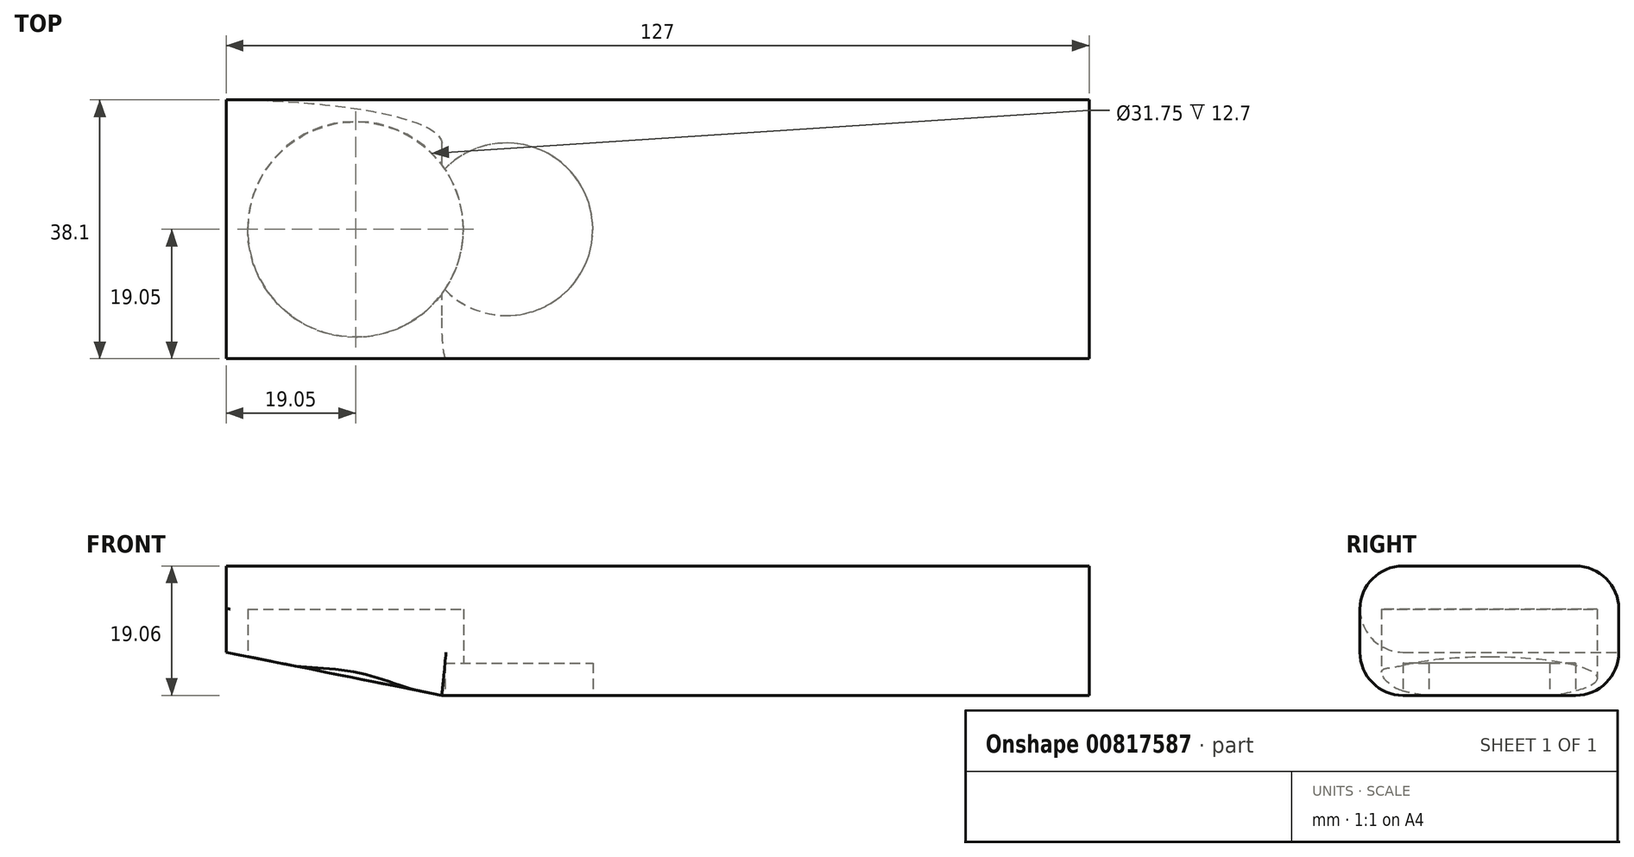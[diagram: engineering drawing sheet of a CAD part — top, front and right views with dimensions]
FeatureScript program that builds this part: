
annotation { "Feature Type Name" : "Feature", "Feature Type Description" : "" }
export const myFeature = defineFeature(function(context is Context, id is Id, definition is map)
    precondition{}
    {
        {
            var Q0;
            Q0=qCreatedBy(makeId("Top.planeOp"),FACE);
            var sketch = newSketch(context, id + "F0", { "sketchPlane" : qUnion([Q0])});
            skLineSegment(sketch, "E0.bottom", {"start": v(-63.5, 19.05) * mm, "end": v(63.5, 19.05) * mm});
            skLineSegment(sketch, "E0.top", {"start": v(-63.5, -19.05) * mm, "end": v(63.5, -19.05) * mm});
            skLineSegment(sketch, "E0.left", {"start": v(-63.5, 19.05) * mm, "end": v(-63.5, -19.05) * mm});
            skLineSegment(sketch, "E0.right", {"start": v(63.5, 19.05) * mm, "end": v(63.5, -19.05) * mm});
            skLineSegment(sketch, "E1", {"start": v(-63.5, 19.05) * mm, "end": v(63.5, -19.05) * mm, "construction": true});
            skSolve(sketch);
        }
        {
            var Q0;
            Q0 = qSketchRegion(id + "F0", true);
            extrude(context, id + "F1", {"entities" : qUnion([Q0]), "endBound" : BoundingType.SYMMETRIC, "depth" : 19.05 * mm, "offsetDistance" : 25.4 * mm});
        }
        {
            var Q0;
            Q0=makeQuery(id+"F1.opExtrude","CAP_FACE",FACE,{"disambiguationData":[OSD([sQuery(id+"F0.wireOp",EDGE,"E0.bottom"),sQuery(id+"F0.wireOp",EDGE,"E0.top"),sQuery(id+"F0.wireOp",EDGE,"E0.left"),sQuery(id+"F0.wireOp",EDGE,"E0.right")])],"isStart":true});
            var sketch = newSketch(context, id + "F2", { "sketchPlane" : qUnion([Q0])});
            skCircle(sketch, "E2", {"center": v(-44.45, 0) * mm, "radius": 15.88 * mm});
            skSolve(sketch);
        }
        {
            var Q0;
            Q0 = qSketchRegion(id + "F2", true);
            extrude(context, id + "F3", {"entities" : qUnion([Q0]), "operationType" : NewBodyOperationType.REMOVE, "oppositeDirection" : true, "depth" : 12.7 * mm, "offsetDistance" : 25.4 * mm});
        }
        {
            var Q0;
            Q0=makeQuery(id+"F1.opExtrude","CAP_FACE",FACE,{"disambiguationData":[OSD([sQuery(id+"F0.wireOp",EDGE,"E0.bottom"),sQuery(id+"F0.wireOp",EDGE,"E0.top"),sQuery(id+"F0.wireOp",EDGE,"E0.left"),sQuery(id+"F0.wireOp",EDGE,"E0.right")])],"isStart":true});
            var sketch = newSketch(context, id + "F4", { "sketchPlane" : qUnion([Q0])});
            skCircle(sketch, "E3", {"center": v(-22.23, 0) * mm, "radius": 12.7 * mm});
            skCircle(sketch, "E4", {"center": v(-47.63, 0) * mm, "radius": 12.7 * mm, "construction": true});
            skSolve(sketch);
        }
        {
            var Q0;
            {var subQ0=sQuery(id+"F4.wireOp",EDGE,"E3");var subQ1=makeQuery(id+"F3.boolean.opBoolean","COPY",EDGE,{"derivedFrom":makeQuery(id+"F3.opExtrude","CAP_EDGE",EDGE,{"disambiguationData":[OSD([sQuery(id+"F2.wireOp",EDGE,"E2")])],"isStart":true})});var subQ2=makeQuery(id+"F4.imprint","INTERSECT",VERTEX,{"disambiguationData":[OD(0.0)],"derivedFrom":[subQ1,subQ0]});Q0=makeQuery(id+"F4.imprint","IMPRINT",FACE,{"disambiguationData":[TD([[makeQuery(id+"F4.imprint","IMPRINT",EDGE,{"disambiguationData":[TD([[subQ2,1.0]])],"derivedFrom":subQ0}),1.0]])]});}
            extrude(context, id + "F5", {"entities" : qUnion([Q0]), "operationType" : NewBodyOperationType.REMOVE, "oppositeDirection" : true, "depth" : 4.76 * mm, "offsetDistance" : 25.4 * mm});
        }
        {
            var Q0;
            Q0=makeQuery(id+"F1.opExtrude","SWEPT_FACE",FACE,{"disambiguationData":[OSD([sQuery(id+"F0.wireOp",EDGE,"E0.bottom")])]});
            var sketch = newSketch(context, id + "F6", { "sketchPlane" : qUnion([Q0])});
            skLineSegment(sketch, "E5", {"start": v(63.5, -9.53) * mm, "end": v(31.75, -9.53) * mm});
            skLineSegment(sketch, "E6", {"start": v(31.75, -9.53) * mm, "end": v(63.5, -3.18) * mm});
            skLineSegment(sketch, "E7", {"start": v(63.5, -3.17) * mm, "end": v(63.5, -9.53) * mm});
            skSolve(sketch);
        }
        {
            var Q0;
            Q0 = qSketchRegion(id + "F6", true);
            extrude(context, id + "F7", {"entities" : qUnion([Q0]), "operationType" : NewBodyOperationType.REMOVE, "endBound" : BoundingType.THROUGH_ALL, "oppositeDirection" : true, "depth" : 25.4 * mm, "offsetDistance" : 25.4 * mm});
        }
        {
            var Q0;
            Q0=makeQuery(id+"F1.opExtrude","CAP_EDGE",EDGE,{"disambiguationData":[OSD([sQuery(id+"F0.wireOp",EDGE,"E0.top")])],"isStart":false});
            var Q1;
            Q1=makeQuery(id+"F1.opExtrude","CAP_EDGE",EDGE,{"disambiguationData":[OSD([sQuery(id+"F0.wireOp",EDGE,"E0.bottom")])],"isStart":false});
            var Q2;
            Q2=makeQuery(id+"F1.opExtrude","CAP_EDGE",EDGE,{"disambiguationData":[OSD([sQuery(id+"F0.wireOp",EDGE,"E0.top")])],"isStart":true});
            var Q3;
            Q3=makeQuery(id+"F1.opExtrude","CAP_EDGE",EDGE,{"disambiguationData":[OSD([sQuery(id+"F0.wireOp",EDGE,"E0.bottom")])],"isStart":true});
            var Q4;
            Q4=makeQuery(id+"F7.boolean.opBoolean","COPY",EDGE,{"derivedFrom":makeQuery(id+"F7.opExtrude","CAP_EDGE",EDGE,{"disambiguationData":[OSD([sQuery(id+"F6.wireOp",EDGE,"E6")])],"isStart":true})});
            var Q5;
            Q5=makeQuery(id+"F7.boolean.opBoolean","INTERSECT",EDGE,{"derivedFrom":[makeQuery(id+"F1.opExtrude","SWEPT_FACE",FACE,{"disambiguationData":[OSD([sQuery(id+"F0.wireOp",EDGE,"E0.top")])]}),makeQuery(id+"F7.opExtrude","SWEPT_FACE",FACE,{"disambiguationData":[OSD([sQuery(id+"F6.wireOp",EDGE,"E6")])]})]});
            fillet(context, id + "F8", {"entities" : qUnion([Q0, Q1, Q2, Q3, Q4, Q5]), "radius" : 6.35 * mm, "tangentPropagation" : true, "allowEdgeOverflow" : false});
        }
    });
